# Revit family: xShowerhead-American_Standard-Spectra_eTouch-1698.474
name_source: partatom
category: Plumbing Fixtures
revit_build: Autodesk Revit 2014 (Build: 20130308_1515(x64)
units: mm (PartAtom-declared; Revit-internal decimal feet)

## types (1)
- 1698.474
    Assembly Code = D2010710
    CW Connection = Yes
    CWFU = 3
    Default Elevation = 0"
    Description = Spectra eTouch 4-Function Showerhead with Remote
    Finish = Brass-American Standard-002-Polished Chrome
    Flow Rate = 1.8 gpm/ 6.8 L/min.
    HW Connection = Yes
    HWFU = 3
    Height = 4 3/16"
    Installation Type = Wall Mounted
    Length = 7 3/16"
    Manufacturer = American Standard
    Material = Brass-American Standard-002-Polished Chrome
    Model = 1698.474
    Price = Prices may vary. Please consult Manufacturer Representative for most up-to-date price list.
    Product Documentation Link = https://www.americanstandard-us.com
    Product Page URL = https://www.americanstandard-us.com
    Shower Remote = Yes
    Specification = Showerhead shall feature 4 spray functions with maximum 1.8 gpm/6.8 L/min flow rate
    URL = https://www.americanstandard-us.com
    Vent Connection = No
    WFU = 4
    Warranty Information = One Year General Product Warranty
    Waste Connection = No
    Water Connection Diameter = 1/2"
    Water Connection Radius = 1/4"
    Width = 7 3/16"

## geometry (parser evidence)
native form markers: Sweep x1
no freeform markers — native parametric forms only
